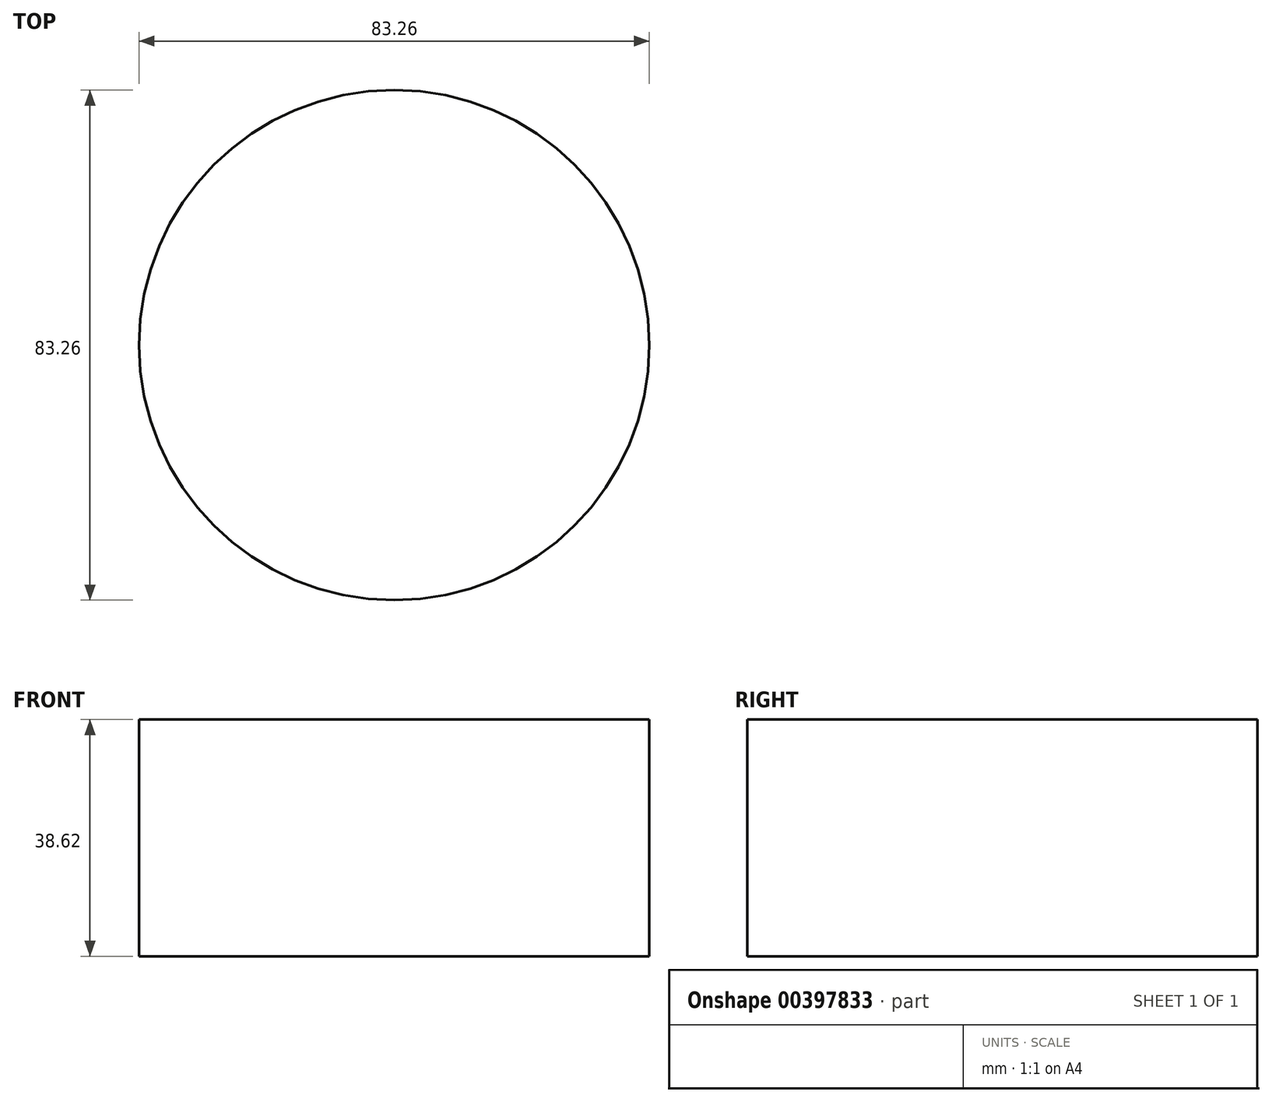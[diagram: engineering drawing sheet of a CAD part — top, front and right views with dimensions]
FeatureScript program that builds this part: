
annotation { "Feature Type Name" : "Feature", "Feature Type Description" : "" }
export const myFeature = defineFeature(function(context is Context, id is Id, definition is map)
    precondition{}
    {
        {
            var Q0;
            Q0=qCreatedBy(makeId("Front.planeOp"),FACE);
            var sketch = newSketch(context, id + "F0", { "sketchPlane" : qUnion([Q0])});
            skLineSegment(sketch, "E0.bottom", {"start": v(-41.63, 38.62) * mm, "end": v(0, 38.62) * mm});
            skLineSegment(sketch, "E0.top", {"start": v(-41.63, 0) * mm, "end": v(0, 0) * mm});
            skLineSegment(sketch, "E0.left", {"start": v(-41.63, 38.62) * mm, "end": v(-41.63, 0) * mm});
            skLineSegment(sketch, "E0.right", {"start": v(0, 38.62) * mm, "end": v(0, 0) * mm});
            skSolve(sketch);
        }
        {
            var Q0;
            Q0=sQuery(id+"F0.wireOp",EDGE,"E0.bottom");
            var Q1;
            Q1=sQuery(id+"F0.wireOp",EDGE,"E0.left");
            var Q2;
            Q2=sQuery(id+"F0.wireOp",EDGE,"E0.top");
            var Q3;
            Q3=sQuery(id+"F0.wireOp",EDGE,"E0.right");
            revolve(context, id + "F1", {"bodyType" : ToolBodyType.SURFACE, "surfaceEntities" : qUnion([Q0, Q1, Q2]), "axis" : qUnion([Q3]), "revolveType" : RevolveType.FULL});
        }
    });
